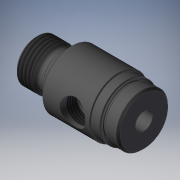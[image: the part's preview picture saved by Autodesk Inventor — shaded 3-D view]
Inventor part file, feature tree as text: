
AUTODESK INVENTOR PART (.ipt)
format: ipt  version: 2019 (Build 230136000, 136)  size: 294,912 bytes
history: native  units: in
note: dims shown in document units (in); Inventor stores cm internally (conversion verified against a paired STEP export)
features: other x119, sketch x6, revolve x5, thread x2, hole x1
ambient origin geometry x8: Origin, YZ Plane, XZ Plane, XY Plane, X Axis, Y Axis, Z Axis, Center Point
bodies: Solid1 (feature_tree)
feature tree (133):
  revolve  "Revolution1"  [1 undecoded]
  thread  "Thread1"  [1 undecoded]
  revolve  "Revolution2"  Angle=360.0deg
  hole  "Hole1"  [1 undecoded]
  revolve  "Revolution3"  [1 undecoded]
  revolve  "Revolution4"  [1 undecoded]
  thread  "Thread2"  [1 undecoded]
  revolve  "Revolution5"  [1 undecoded]
  other  "dp1_XY"
  other  "dp1_YZ"
  other  "dp1_ZX"
  other  "dp1_X"
  other  "dp1_Y"
  other  "dp1_Z"
  other  "dp1_Center"
  other  "dp2_XY"
  other  "dp2_YZ"
  other  "dp2_ZX"
  other  "dp2_X"
  other  "dp2_Y"
  other  "dp2_Z"
  other  "dp2_Center"
  other  "hh_XY"
  other  "hh_YZ"
  other  "hh_ZX"
  other  "hh_X"
  other  "hh_Y"
  other  "hh_Z"
  other  "hh_Center"
  other  "port_XY"
  other  "port_YZ"
  other  "port_ZX"
  other  "port_X"
  other  "port_Y"
  other  "port_Z"
  other  "port_Center"
  other  "rod_guide_XY"
  other  "rod_guide_YZ"
  other  "rod_guide_ZX"
  other  "rod_guide_X"
  other  "rod_guide_Y"
  other  "rod_guide_Z"
  other  "rod_guide_Center"
  other  "s1_XY"
  other  "s1_YZ"
  other  "s1_ZX"
  other  "s1_X"
  other  "s1_Y"
  other  "s1_Z"
  other  "s1_Center"
  other  "s2_XY"
  other  "s2_YZ"
  other  "s2_ZX"
  other  "s2_X"
  other  "s2_Y"
  other  "s2_Z"
  other  "s2_Center"
  other  "t1_XY"
  other  "t1_YZ"
  other  "t1_ZX"
  other  "t1_X"
  other  "t1_Y"
  other  "t1_Z"
  other  "t1_Center"
  other  "t111_XY"
  other  "t111_YZ"
  other  "t111_ZX"
  other  "t111_X"
  other  "t111_Y"
  other  "t111_Z"
  other  "t111_Center"
  other  "to_foot_bracket_XY"
  other  "to_foot_bracket_YZ"
  other  "to_foot_bracket_ZX"
  other  "to_foot_bracket_X"
  other  "to_foot_bracket_Y"
  other  "to_foot_bracket_Z"
  other  "to_foot_bracket_Center"
  other  "to_nut_XY"
  other  "to_nut_YZ"
  other  "to_nut_ZX"
  other  "to_nut_X"
  other  "to_nut_Y"
  other  "to_nut_Z"
  other  "to_nut_Center"
  other  "to_rod_XY"
  other  "to_rod_YZ"
  other  "to_rod_ZX"
  other  "to_rod_X"
  other  "to_rod_Y"
  other  "to_rod_Z"
  other  "to_rod_Center"
  other  "to_screw_XY"
  other  "to_screw_YZ"
  other  "to_screw_ZX"
  other  "to_screw_X"
  other  "to_screw_Y"
  other  "to_screw_Z"
  other  "to_screw_Center"
  other  "to_trunnion_brackets_XY"
  other  "to_trunnion_brackets_YZ"
  other  "to_trunnion_brackets_ZX"
  other  "to_trunnion_brackets_X"
  other  "to_trunnion_brackets_Y"
  other  "to_trunnion_brackets_Z"
  other  "to_trunnion_brackets_Center"
  other  "to_trunnion_brackets1_XY"
  other  "to_trunnion_brackets1_YZ"
  other  "to_trunnion_brackets1_ZX"
  other  "to_trunnion_brackets1_X"
  other  "to_trunnion_brackets1_Y"
  other  "to_trunnion_brackets1_Z"
  other  "to_trunnion_brackets1_Center"
  other  "to_trunnion_brackets2_XY"
  other  "to_trunnion_brackets2_YZ"
  other  "to_trunnion_brackets2_ZX"
  other  "to_trunnion_brackets2_X"
  other  "to_trunnion_brackets2_Y"
  other  "to_trunnion_brackets2_Z"
  other  "to_trunnion_brackets2_Center"
  other  "to_tube_XY"
  other  "to_tube_YZ"
  other  "to_tube_ZX"
  other  "to_tube_X"
  other  "to_tube_Y"
  other  "to_tube_Z"
  other  "to_tube_Center"
  sketch  "Sketch_2"  dims[d0=360.0deg d1=0.23in d2=0.0in d3=360.0deg]
  sketch  "Sketch_3"  dims[d4=0.2535in d5=0.75in d6=0.2735in d7=0.25in d8=90.0deg d9=1.594in d10=0.0in d11=360.0deg]
  sketch  "Sketch3"  dims[d12=360.0deg d13=0.1501in d14=0.0in]
  sketch  "Sketch_10"  dims[d15=360.0deg]
  sketch  "Sketch_40"  dims[d16=0.0in d17=0.0in d18=0.0in d19=0.0in d20=0.0in d21=0.0in]
  sketch  "Sketch_47"
note: 7 required parameter values undecoded (feature->parameter linkage not recoverable at this tier; creation-order binding heuristic only, values carry confidence <= 0.55)